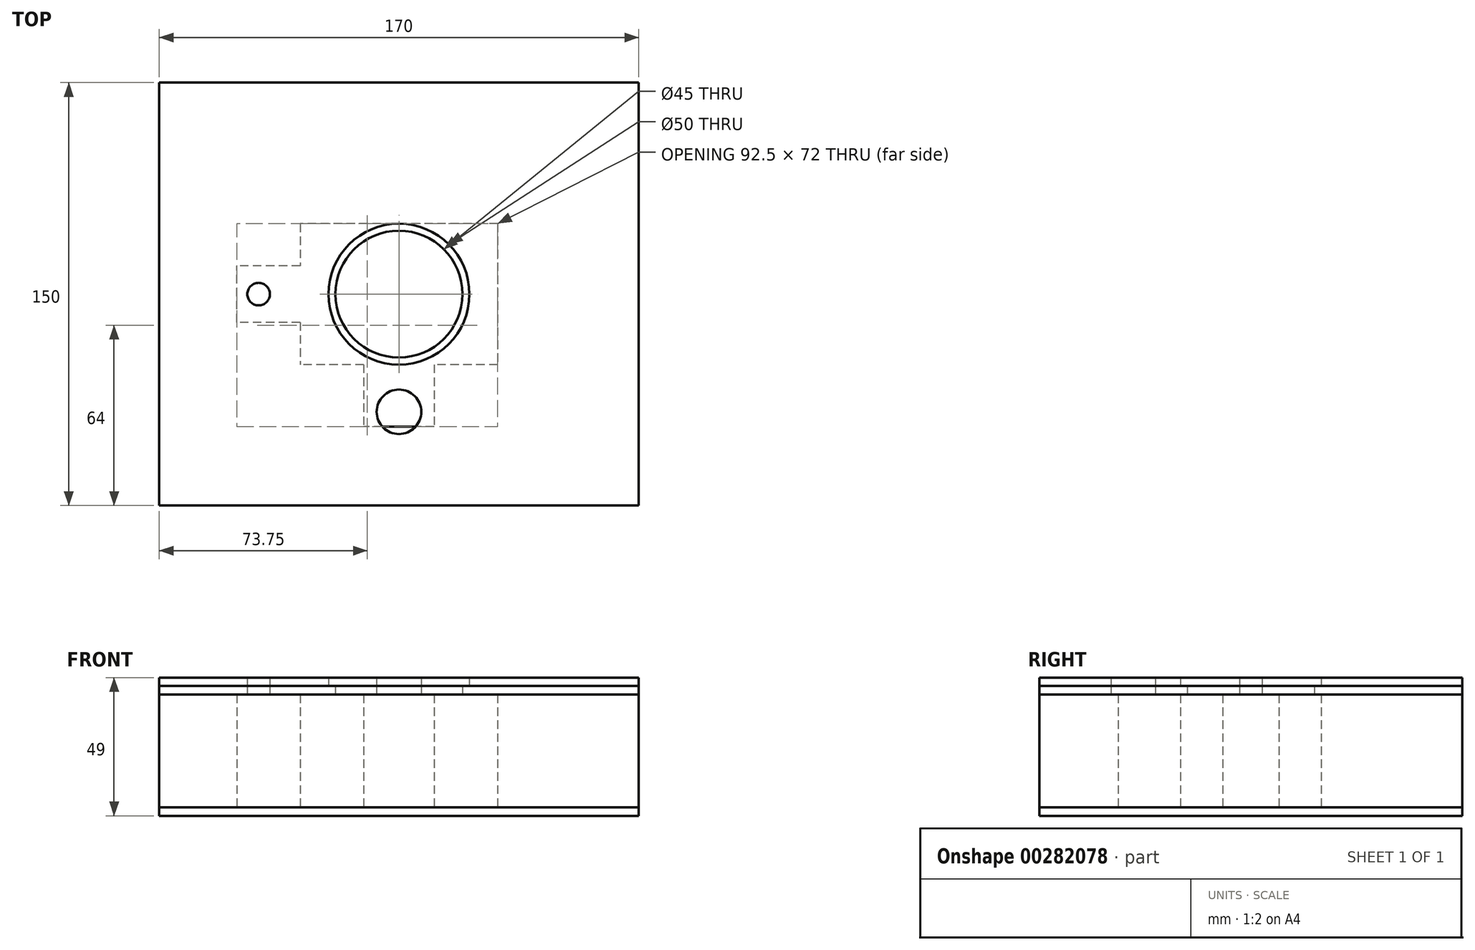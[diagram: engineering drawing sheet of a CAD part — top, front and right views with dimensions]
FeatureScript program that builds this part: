
annotation { "Feature Type Name" : "Feature", "Feature Type Description" : "" }
export const myFeature = defineFeature(function(context is Context, id is Id, definition is map)
    precondition{}
    {
        {
            var Q0;
            Q0=qCreatedBy(makeId("Top.planeOp"),FACE);
            var sketch = newSketch(context, id + "F0", { "sketchPlane" : qUnion([Q0])});
            skLineSegment(sketch, "E0.bottom", {"start": v(85, 75) * mm, "end": v(-85, 75) * mm});
            skLineSegment(sketch, "E0.top", {"start": v(85, -75) * mm, "end": v(-85, -75) * mm});
            skLineSegment(sketch, "E0.left", {"start": v(85, 75) * mm, "end": v(85, -75) * mm});
            skLineSegment(sketch, "E0.right", {"start": v(-85, 75) * mm, "end": v(-85, -75) * mm});
            skPoint(sketch, "E0.middle", {"position": v(0, 0) * mm});
            skLineSegment(sketch, "E1.bottom", {"start": v(35, 25) * mm, "end": v(-35, 25) * mm});
            skLineSegment(sketch, "E1.top", {"start": v(35, -25) * mm, "end": v(12.5, -25) * mm});
            skLineSegment(sketch, "E1.left", {"start": v(35, 25) * mm, "end": v(35, -25) * mm});
            skLineSegment(sketch, "E1.right", {"start": v(-35, 25) * mm, "end": v(-35, 10) * mm});
            skLineSegment(sketch, "E2.top", {"start": v(12.5, -47) * mm, "end": v(-12.5, -47) * mm});
            skLineSegment(sketch, "E2.left", {"start": v(12.5, -25) * mm, "end": v(12.5, -47) * mm});
            skLineSegment(sketch, "E2.right", {"start": v(-12.5, -25) * mm, "end": v(-12.5, -47) * mm});
            skPoint(sketch, "E2.middle", {"position": v(0, -36) * mm});
            skPoint(sketch, "E2.middle.positionSnap0", {"position": v(0, -25) * mm});
            skPoint(sketch, "E2.centerSnap0", {"position": v(0, -25) * mm});
            skLineSegment(sketch, "E3.bottom", {"start": v(-35, -10) * mm, "end": v(-57.5, -10) * mm});
            skLineSegment(sketch, "E3.top", {"start": v(-35, 10) * mm, "end": v(-57.5, 10) * mm});
            skLineSegment(sketch, "E3.right", {"start": v(-57.5, -10) * mm, "end": v(-57.5, 10) * mm});
            skPoint(sketch, "E3.middle", {"position": v(-46.25, 0) * mm});
            skLineSegment(sketch, "E4.trimOffspring", {"start": v(-35, -10) * mm, "end": v(-35, -25) * mm});
            skLineSegment(sketch, "E5.trimOffspring", {"start": v(-12.5, -25) * mm, "end": v(-35, -25) * mm});
            skSolve(sketch);
        }
        {
            var Q0;
            Q0=makeQuery(id+"F0.imprint","IMPRINT",FACE,{"disambiguationData":[TD([[makeQuery(id+"F0.imprint","IMPRINT",EDGE,{"derivedFrom":sQuery(id+"F0.wireOp",EDGE,"E0.bottom")}),1.0]])]});
            extrude(context, id + "F1", {"entities" : qUnion([Q0]), "depth" : 40 * mm});
        }
        {
            var Q0;
            Q0=makeQuery(id+"F1.opExtrude","CAP_FACE",FACE,{"disambiguationData":[OSD([sQuery(id+"F0.wireOp",EDGE,"E0.bottom"),sQuery(id+"F0.wireOp",EDGE,"E0.top"),sQuery(id+"F0.wireOp",EDGE,"E0.left"),sQuery(id+"F0.wireOp",EDGE,"E0.right"),sQuery(id+"F0.wireOp",EDGE,"E1.bottom"),sQuery(id+"F0.wireOp",EDGE,"E1.top"),sQuery(id+"F0.wireOp",EDGE,"E1.left"),sQuery(id+"F0.wireOp",EDGE,"E1.right"),sQuery(id+"F0.wireOp",EDGE,"E2.top"),sQuery(id+"F0.wireOp",EDGE,"E2.left"),sQuery(id+"F0.wireOp",EDGE,"E2.right"),sQuery(id+"F0.wireOp",EDGE,"E3.bottom"),sQuery(id+"F0.wireOp",EDGE,"E3.top"),sQuery(id+"F0.wireOp",EDGE,"E3.right"),sQuery(id+"F0.wireOp",EDGE,"E4.trimOffspring"),sQuery(id+"F0.wireOp",EDGE,"E5.trimOffspring")])],"isStart":true});
            var sketch = newSketch(context, id + "F2", { "sketchPlane" : qUnion([Q0])});
            skLineSegment(sketch, "E6.0", {"start": v(85, 75) * mm, "end": v(-85, 75) * mm});
            skLineSegment(sketch, "E7.0", {"start": v(85, -75) * mm, "end": v(85, 75) * mm});
            skLineSegment(sketch, "E8.0", {"start": v(85, -75) * mm, "end": v(-85, -75) * mm});
            skLineSegment(sketch, "E9.0", {"start": v(-85, -75) * mm, "end": v(-85, 75) * mm});
            skSolve(sketch);
        }
        {
            var Q0;
            Q0 = qSketchRegion(id + "F2", true);
            extrude(context, id + "F3", {"entities" : qUnion([Q0]), "depth" : 3 * mm});
        }
        {
            var Q0;
            Q0=makeQuery(id+"F1.opExtrude","CAP_FACE",FACE,{"disambiguationData":[OSD([sQuery(id+"F0.wireOp",EDGE,"E0.bottom"),sQuery(id+"F0.wireOp",EDGE,"E0.top"),sQuery(id+"F0.wireOp",EDGE,"E0.left"),sQuery(id+"F0.wireOp",EDGE,"E0.right"),sQuery(id+"F0.wireOp",EDGE,"E1.bottom"),sQuery(id+"F0.wireOp",EDGE,"E1.top"),sQuery(id+"F0.wireOp",EDGE,"E1.left"),sQuery(id+"F0.wireOp",EDGE,"E1.right"),sQuery(id+"F0.wireOp",EDGE,"E2.top"),sQuery(id+"F0.wireOp",EDGE,"E2.left"),sQuery(id+"F0.wireOp",EDGE,"E2.right"),sQuery(id+"F0.wireOp",EDGE,"E3.bottom"),sQuery(id+"F0.wireOp",EDGE,"E3.top"),sQuery(id+"F0.wireOp",EDGE,"E3.right"),sQuery(id+"F0.wireOp",EDGE,"E4.trimOffspring"),sQuery(id+"F0.wireOp",EDGE,"E5.trimOffspring")])],"isStart":false});
            var sketch = newSketch(context, id + "F4", { "sketchPlane" : qUnion([Q0])});
            skLineSegment(sketch, "E10.0", {"start": v(85, 75) * mm, "end": v(-85, 75) * mm});
            skLineSegment(sketch, "E11.0", {"start": v(-85, 75) * mm, "end": v(-85, -75) * mm});
            skLineSegment(sketch, "E12.0", {"start": v(85, 75) * mm, "end": v(85, -75) * mm});
            skLineSegment(sketch, "E13.0", {"start": v(85, -75) * mm, "end": v(-85, -75) * mm});
            skCircle(sketch, "E14", {"center": v(0, 0) * mm, "radius": 22.5 * mm});
            skCircle(sketch, "E15", {"center": v(-49.77, 0) * mm, "radius": 4 * mm});
            skCircle(sketch, "E16", {"center": v(0, -41.74) * mm, "radius": 7.9 * mm});
            skSolve(sketch);
        }
        {
            var Q0;
            Q0 = qSketchRegion(id + "F4", true);
            extrude(context, id + "F5", {"entities" : qUnion([Q0]), "depth" : 3 * mm});
        }
        {
            var Q0;
            Q0=makeQuery(id+"F5.opExtrude","CAP_FACE",FACE,{"disambiguationData":[OSD([sQuery(id+"F4.wireOp",EDGE,"E10.0"),sQuery(id+"F4.wireOp",EDGE,"E11.0"),sQuery(id+"F4.wireOp",EDGE,"E12.0"),sQuery(id+"F4.wireOp",EDGE,"E13.0"),sQuery(id+"F4.wireOp",EDGE,"E14"),sQuery(id+"F4.wireOp",EDGE,"E15"),sQuery(id+"F4.wireOp",EDGE,"E16")])],"isStart":false});
            var sketch = newSketch(context, id + "F6", { "sketchPlane" : qUnion([Q0])});
            skLineSegment(sketch, "E17.0", {"start": v(85, 75) * mm, "end": v(-85, 75) * mm});
            skLineSegment(sketch, "E18.0", {"start": v(-85, 75) * mm, "end": v(-85, -75) * mm});
            skLineSegment(sketch, "E19.0", {"start": v(85, 75) * mm, "end": v(85, -75) * mm});
            skLineSegment(sketch, "E20.0", {"start": v(85, -75) * mm, "end": v(-85, -75) * mm});
            skCircle(sketch, "E21", {"center": v(0, 0) * mm, "radius": 25 * mm});
            skCircle(sketch, "E22.0", {"center": v(0, -41.74) * mm, "radius": 7.9 * mm});
            skCircle(sketch, "E23.0", {"center": v(-49.77, 0) * mm, "radius": 4 * mm});
            skSolve(sketch);
        }
        {
            var Q0;
            Q0 = qSketchRegion(id + "F6", true);
            extrude(context, id + "F7", {"entities" : qUnion([Q0]), "depth" : 3 * mm});
        }
    });
